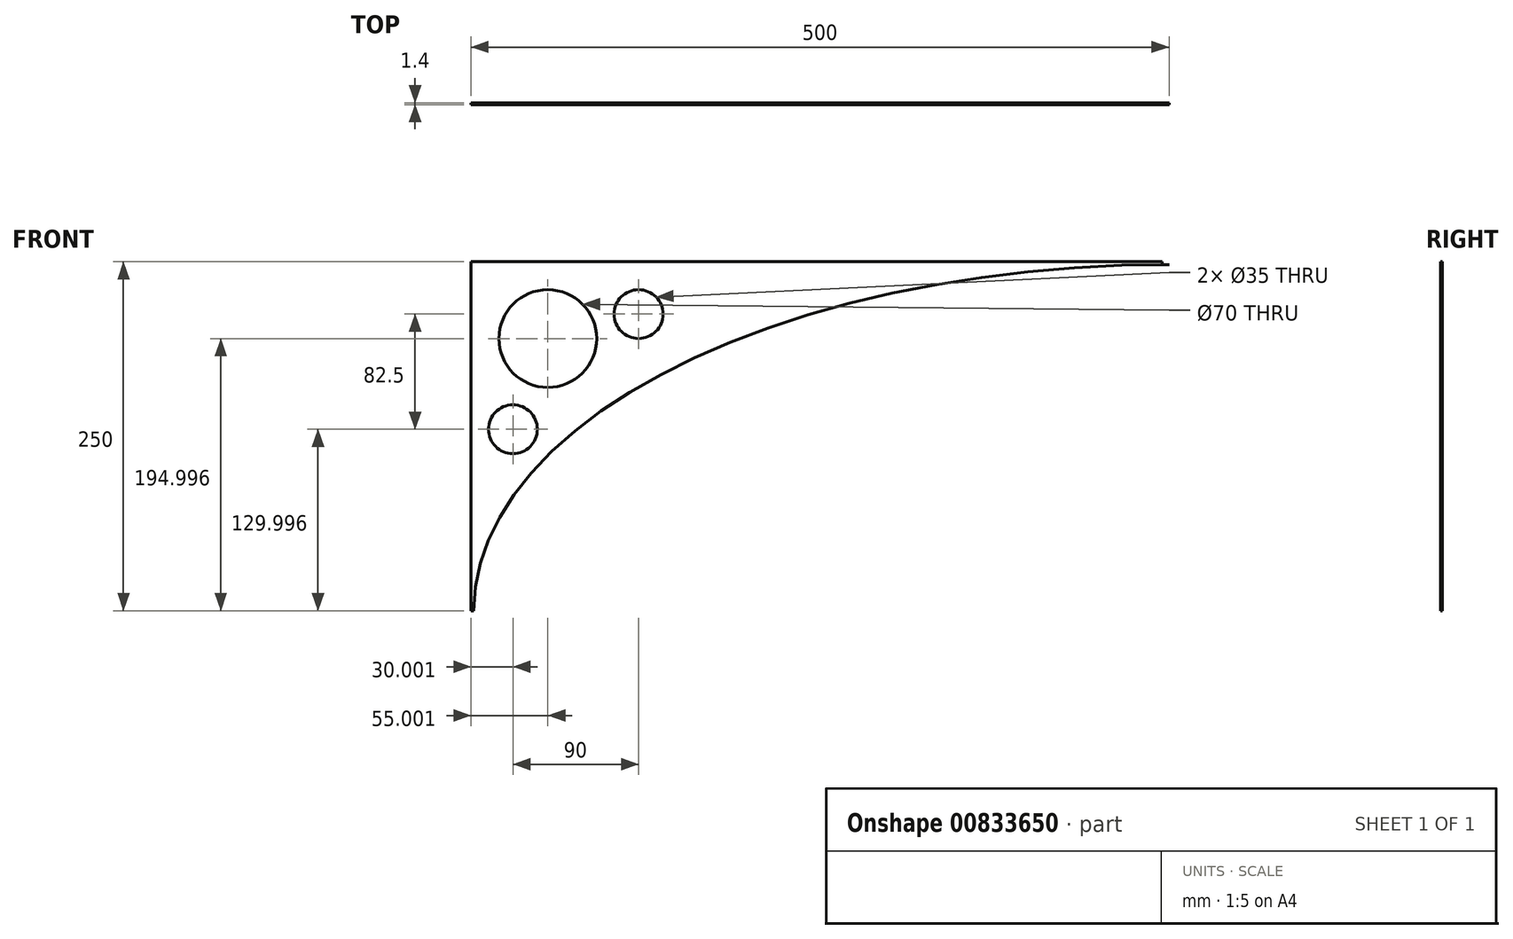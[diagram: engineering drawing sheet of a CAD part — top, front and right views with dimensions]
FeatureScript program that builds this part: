
annotation { "Feature Type Name" : "Feature", "Feature Type Description" : "" }
export const myFeature = defineFeature(function(context is Context, id is Id, definition is map)
    precondition{}
    {
        {
            var Q0;
            Q0=qCreatedBy(makeId("Front.planeOp"),FACE);
            var sketch = newSketch(context, id + "F0", { "sketchPlane" : qUnion([Q0])});
            skLineSegment(sketch, "E0", {"start": v(-265.69, 164.73) * mm, "end": v(234.31, 164.73) * mm});
            skLineSegment(sketch, "E1", {"start": v(234.31, 164.73) * mm, "end": v(234.31, 162.73) * mm});
            skLineSegment(sketch, "E2", {"start": v(-265.69, 164.73) * mm, "end": v(-265.69, -85.27) * mm});
            skLineSegment(sketch, "E3", {"start": v(-265.69, -85.27) * mm, "end": v(-263.69, -85.27) * mm});
            skEllipticalArc(sketch, "E4", {});
            const initialGuessF0  = {"E4": [0.2343109268695116, -0.08527348190546036, -1, 0, 0.498, 0.248, 4.71238898038469, 0]};
            skSetInitialGuess(sketch, initialGuessF0);
            skSolve(sketch);
        }
        {
            var Q0;
            Q0=makeQuery(id+"F0.imprint","IMPRINT",FACE,{"disambiguationData":[TD([[makeQuery(id+"F0.imprint","IMPRINT",EDGE,{"derivedFrom":sQuery(id+"F0.wireOp",EDGE,"E0")}),-1.0]])]});
            extrude(context, id + "F1", {"entities" : qUnion([Q0]), "depth" : 1.4 * mm, "offsetDistance" : 25 * mm});
        }
        {
            var Q0;
            Q0=makeQuery(id+"F1.opExtrude","CAP_FACE",FACE,{"disambiguationData":[OSD([sQuery(id+"F0.wireOp",EDGE,"E0"),sQuery(id+"F0.wireOp",EDGE,"E1"),sQuery(id+"F0.wireOp",EDGE,"E2"),sQuery(id+"F0.wireOp",EDGE,"E3"),sQuery(id+"F0.wireOp",EDGE,"E4")])],"isStart":false});
            var sketch = newSketch(context, id + "F2", { "sketchPlane" : qUnion([Q0])});
            skCircle(sketch, "E5", {"center": v(-210.69, 109.73) * mm, "radius": 35 * mm});
            skCircle(sketch, "E6", {"center": v(-145.69, 127.23) * mm, "radius": 17.5 * mm});
            skLineSegment(sketch, "E7", {"start": v(-210.69, 109.73) * mm, "end": v(-210.69, 164.73) * mm});
            skCircle(sketch, "E8", {"center": v(-235.69, 44.73) * mm, "radius": 17.5 * mm});
            skLineSegment(sketch, "E9", {"start": v(-210.69, 109.73) * mm, "end": v(-265.69, 109.73) * mm});
            skSolve(sketch);
        }
        {
            var Q0;
            Q0=sQuery(id+"F2.wireOp",VERTEX,"E5.center");
            var Q1;
            Q1=makeQuery(id+"F1.opExtrude","SWEPT_BODY",BODY,{"disambiguationData":[OSD([sQuery(id+"F0.wireOp",EDGE,"E0"),sQuery(id+"F0.wireOp",EDGE,"E1"),sQuery(id+"F0.wireOp",EDGE,"E2"),sQuery(id+"F0.wireOp",EDGE,"E3"),sQuery(id+"F0.wireOp",EDGE,"E4")])]});
            hole(context, id + "F3", {"style" : HoleStyle.SIMPLE, "endStyle" : HoleEndStyle.THROUGH, "holeDiameter" : 70 * mm, "majorDiameter" : 5 * mm, "isTappedThrough" : true, "tappedDepth" : 12 * mm, "tapClearance" : 3, "locations" : qUnion([Q0]), "scope" : qUnion([Q1])});
        }
        {
            var Q0;
            Q0=sQuery(id+"F2.wireOp",VERTEX,"E6.center");
            var Q1;
            Q1=sQuery(id+"F2.wireOp",VERTEX,"E8.center");
            var Q2;
            Q2=makeQuery(id+"F1.opExtrude","SWEPT_BODY",BODY,{"disambiguationData":[OSD([sQuery(id+"F0.wireOp",EDGE,"E0"),sQuery(id+"F0.wireOp",EDGE,"E1"),sQuery(id+"F0.wireOp",EDGE,"E2"),sQuery(id+"F0.wireOp",EDGE,"E3"),sQuery(id+"F0.wireOp",EDGE,"E4")])]});
            hole(context, id + "F4", {"style" : HoleStyle.SIMPLE, "endStyle" : HoleEndStyle.THROUGH, "holeDiameter" : 35 * mm, "majorDiameter" : 5 * mm, "isTappedThrough" : true, "tappedDepth" : 12 * mm, "tapClearance" : 3, "locations" : qUnion([Q0, Q1]), "scope" : qUnion([Q2])});
        }
        {
            var Q0;
            Q0=makeQuery(id+"F1.opExtrude","SWEPT_FACE",FACE,{"disambiguationData":[OSD([sQuery(id+"F0.wireOp",EDGE,"E0")])]});
            var sketch = newSketch(context, id + "F5", { "sketchPlane" : qUnion([Q0])});
            skLineSegment(sketch, "E10.bottom", {"start": v(239.31, 4.3) * mm, "end": v(229.31, 4.3) * mm});
            skLineSegment(sketch, "E10.top", {"start": v(239.31, -5.7) * mm, "end": v(229.31, -5.7) * mm});
            skLineSegment(sketch, "E10.left", {"start": v(239.31, 4.3) * mm, "end": v(239.31, -5.7) * mm});
            skLineSegment(sketch, "E10.right", {"start": v(229.31, 4.3) * mm, "end": v(229.31, -5.7) * mm});
            skPoint(sketch, "E10.middle", {"position": v(234.31, -0.7) * mm});
            skLineSegment(sketch, "E11", {"start": v(234.31, 0) * mm, "end": v(229.31, 0) * mm});
            skLineSegment(sketch, "E12", {"start": v(234.31, 0) * mm, "end": v(234.31, -1.4) * mm});
            skLineSegment(sketch, "E13", {"start": v(234.31, -1.4) * mm, "end": v(229.31, -1.4) * mm});
            skLineSegment(sketch, "E14", {"start": v(229.31, -1.4) * mm, "end": v(229.31, -5.7) * mm});
            skSolve(sketch);
        }
        {
            var Q0;
            {var subQ1=sQuery(id+"F5.wireOp",EDGE,"E10.bottom");Q0=makeQuery(id+"F5.imprint","IMPRINT",FACE,{"disambiguationData":[TD([[makeQuery(id+"F5.imprint","IMPRINT",EDGE,{"derivedFrom":subQ1}),1.0]])]});}
            var Q1;
            {var subQ3=sQuery(id+"F5.wireOp",EDGE,"E11");Q1=makeQuery(id+"F5.imprint","IMPRINT",FACE,{"disambiguationData":[TD([[makeQuery(id+"F5.imprint","IMPRINT",EDGE,{"derivedFrom":subQ3}),-1.0]])]});}
            extrude(context, id + "F6", {"entities" : qUnion([Q0, Q1]), "operationType" : NewBodyOperationType.REMOVE, "oppositeDirection" : true, "depth" : 2 * mm, "offsetDistance" : 25 * mm});
        }
    });
